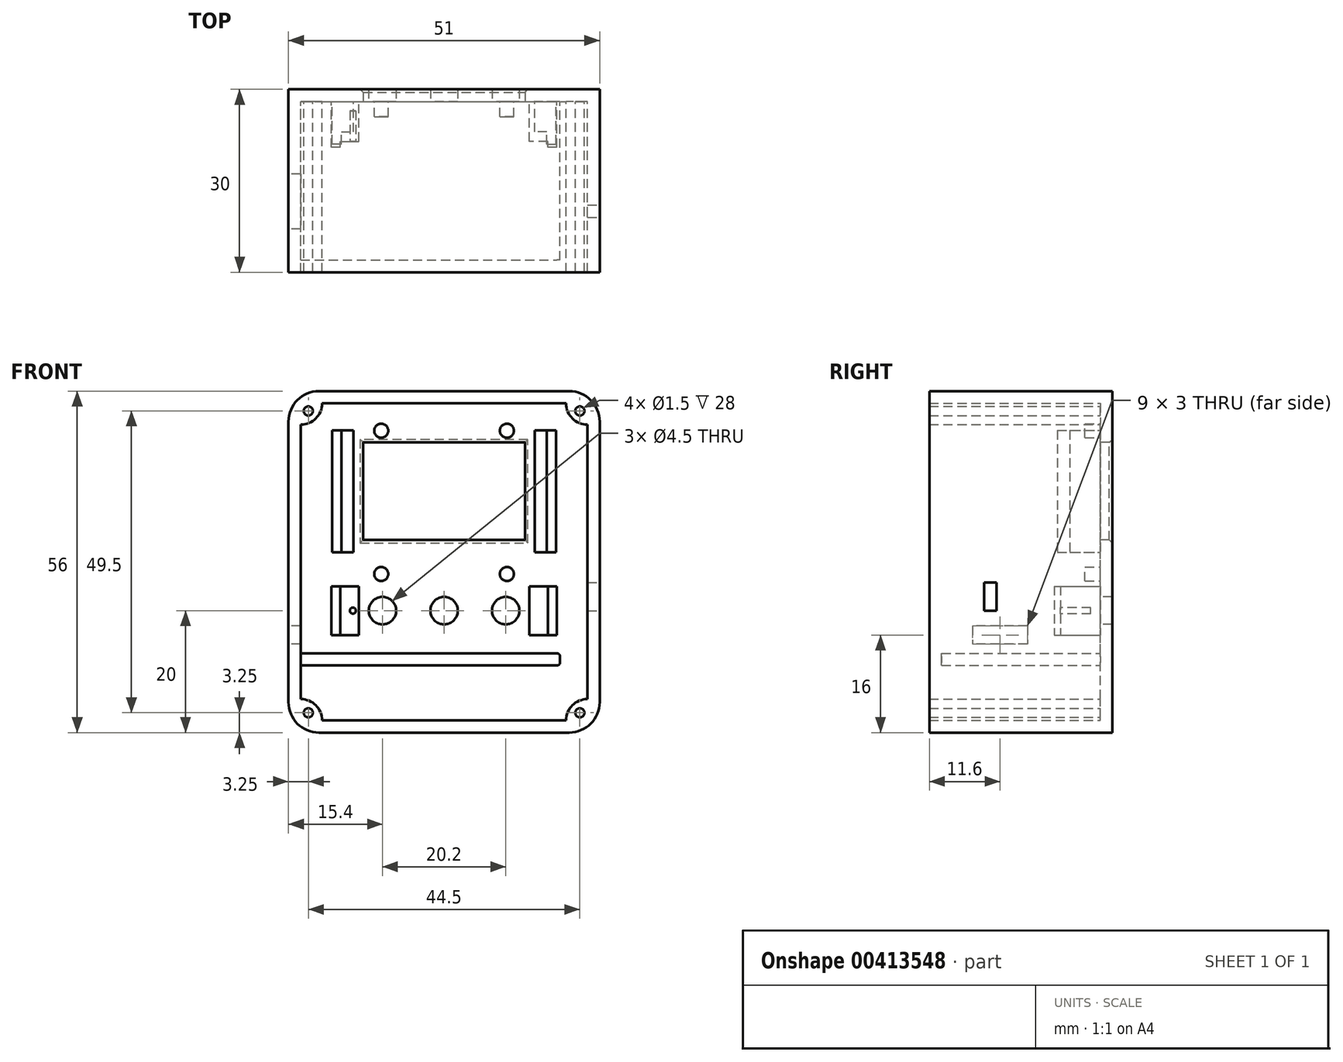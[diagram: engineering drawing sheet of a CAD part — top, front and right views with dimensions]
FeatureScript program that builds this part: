
annotation { "Feature Type Name" : "Feature", "Feature Type Description" : "" }
export const myFeature = defineFeature(function(context is Context, id is Id, definition is map)
    precondition{}
    {
        {
            var Q0;
            Q0=qCreatedBy(makeId("Front.planeOp"),FACE);
            var sketch = newSketch(context, id + "F0", { "sketchPlane" : qUnion([Q0])});
            skLineSegment(sketch, "E0.bottom", {"start": v(0, 0) * mm, "end": v(51, 0) * mm});
            skLineSegment(sketch, "E0.top", {"start": v(0, 56) * mm, "end": v(51, 56) * mm});
            skLineSegment(sketch, "E0.left", {"start": v(0, 0) * mm, "end": v(0, 56) * mm});
            skLineSegment(sketch, "E0.right", {"start": v(51, 0) * mm, "end": v(51, 56) * mm});
            skLineSegment(sketch, "E1", {"start": v(-7.83, 28) * mm, "end": v(58.94, 28) * mm, "construction": true});
            skPoint(sketch, "E1.startSnap0", {"position": v(0, 28) * mm});
            skPoint(sketch, "E1.endSnap0", {"position": v(51, 28) * mm});
            skSolve(sketch);
        }
        {
            var Q0;
            Q0 = qSketchRegion(id + "F0", true);
            extrude(context, id + "F1", {"entities" : qUnion([Q0]), "depth" : 30 * mm});
        }
        {
            var Q0;
            Q0=makeQuery(id+"F1.opExtrude","CAP_FACE",FACE,{"disambiguationData":[OSD([sQuery(id+"F0.wireOp",EDGE,"E0.bottom"),sQuery(id+"F0.wireOp",EDGE,"E0.top"),sQuery(id+"F0.wireOp",EDGE,"E0.left"),sQuery(id+"F0.wireOp",EDGE,"E0.right")])],"isStart":false});
            shell(context, id + "F2", {"entities" : qUnion([Q0]), "thickness" : 2 * mm});
        }
        {
            var Q0;
            Q0=makeQuery(id+"F1.opExtrude","SWEPT_EDGE",EDGE,{"disambiguationData":[OSD([sQuery(id+"F0.wireOp",EDGE,"E0.top"),sQuery(id+"F0.wireOp",EDGE,"E0.left")])]});
            var Q1;
            Q1=makeQuery(id+"F1.opExtrude","SWEPT_EDGE",EDGE,{"disambiguationData":[OSD([sQuery(id+"F0.wireOp",EDGE,"E0.bottom"),sQuery(id+"F0.wireOp",EDGE,"E0.left")])]});
            var Q2;
            Q2=makeQuery(id+"F1.opExtrude","SWEPT_EDGE",EDGE,{"disambiguationData":[OSD([sQuery(id+"F0.wireOp",EDGE,"E0.bottom"),sQuery(id+"F0.wireOp",EDGE,"E0.right")])]});
            var Q3;
            Q3=makeQuery(id+"F1.opExtrude","SWEPT_EDGE",EDGE,{"disambiguationData":[OSD([sQuery(id+"F0.wireOp",EDGE,"E0.top"),sQuery(id+"F0.wireOp",EDGE,"E0.right")])]});
            fillet(context, id + "F3", {"entities" : qUnion([Q0, Q1, Q2, Q3]), "radius" : 5 * mm, "tangentPropagation" : true, "allowEdgeOverflow" : false});
        }
        {
            var Q0;
            Q0=makeQuery(id+"F2.opShell","OFFSET_FACE",FACE,{"disambiguationData":[OSD([sQuery(id+"F0.wireOp",EDGE,"E0.bottom"),sQuery(id+"F0.wireOp",EDGE,"E0.top"),sQuery(id+"F0.wireOp",EDGE,"E0.left"),sQuery(id+"F0.wireOp",EDGE,"E0.right")])]});
            var sketch = newSketch(context, id + "F4", { "sketchPlane" : qUnion([Q0])});
            skLineSegment(sketch, "E2.bottom", {"start": v(12.25, 47.58) * mm, "end": v(38.75, 47.58) * mm});
            skLineSegment(sketch, "E2.top", {"start": v(12.25, 31.58) * mm, "end": v(38.75, 31.58) * mm});
            skLineSegment(sketch, "E2.left", {"start": v(12.25, 47.58) * mm, "end": v(12.25, 31.58) * mm});
            skLineSegment(sketch, "E2.right", {"start": v(38.75, 47.58) * mm, "end": v(38.75, 31.58) * mm});
            skSolve(sketch);
        }
        {
            var Q0;
            Q0=makeQuery(id+"F4.imprint","IMPRINT",FACE,{"disambiguationData":[TD([[makeQuery(id+"F4.imprint","IMPRINT",EDGE,{"derivedFrom":sQuery(id+"F4.wireOp",EDGE,"E2.bottom")}),-1.0]])]});
            extrude(context, id + "F5", {"entities" : qUnion([Q0]), "operationType" : NewBodyOperationType.REMOVE, "endBound" : BoundingType.THROUGH_ALL, "oppositeDirection" : true, "depth" : 25 * mm});
        }
        {
            var Q0;
            Q0=makeQuery(id+"F5.boolean.opBoolean","INTERSECT",EDGE,{"derivedFrom":[makeQuery(id+"F1.opExtrude","CAP_FACE",FACE,{"disambiguationData":[OSD([sQuery(id+"F0.wireOp",EDGE,"E0.bottom"),sQuery(id+"F0.wireOp",EDGE,"E0.top"),sQuery(id+"F0.wireOp",EDGE,"E0.left"),sQuery(id+"F0.wireOp",EDGE,"E0.right")])],"isStart":true}),makeQuery(id+"F5.opExtrude","SWEPT_FACE",FACE,{"disambiguationData":[OSD([sQuery(id+"F4.wireOp",EDGE,"E2.bottom")])]})]});
            var Q1;
            Q1=makeQuery(id+"F5.boolean.opBoolean","INTERSECT",EDGE,{"derivedFrom":[makeQuery(id+"F1.opExtrude","CAP_FACE",FACE,{"disambiguationData":[OSD([sQuery(id+"F0.wireOp",EDGE,"E0.bottom"),sQuery(id+"F0.wireOp",EDGE,"E0.top"),sQuery(id+"F0.wireOp",EDGE,"E0.left"),sQuery(id+"F0.wireOp",EDGE,"E0.right")])],"isStart":true}),makeQuery(id+"F5.opExtrude","SWEPT_FACE",FACE,{"disambiguationData":[OSD([sQuery(id+"F4.wireOp",EDGE,"E2.right")])]})]});
            var Q2;
            Q2=makeQuery(id+"F5.boolean.opBoolean","INTERSECT",EDGE,{"derivedFrom":[makeQuery(id+"F1.opExtrude","CAP_FACE",FACE,{"disambiguationData":[OSD([sQuery(id+"F0.wireOp",EDGE,"E0.bottom"),sQuery(id+"F0.wireOp",EDGE,"E0.top"),sQuery(id+"F0.wireOp",EDGE,"E0.left"),sQuery(id+"F0.wireOp",EDGE,"E0.right")])],"isStart":true}),makeQuery(id+"F5.opExtrude","SWEPT_FACE",FACE,{"disambiguationData":[OSD([sQuery(id+"F4.wireOp",EDGE,"E2.top")])]})]});
            var Q3;
            Q3=makeQuery(id+"F5.boolean.opBoolean","INTERSECT",EDGE,{"derivedFrom":[makeQuery(id+"F1.opExtrude","CAP_FACE",FACE,{"disambiguationData":[OSD([sQuery(id+"F0.wireOp",EDGE,"E0.bottom"),sQuery(id+"F0.wireOp",EDGE,"E0.top"),sQuery(id+"F0.wireOp",EDGE,"E0.left"),sQuery(id+"F0.wireOp",EDGE,"E0.right")])],"isStart":true}),makeQuery(id+"F5.opExtrude","SWEPT_FACE",FACE,{"disambiguationData":[OSD([sQuery(id+"F4.wireOp",EDGE,"E2.left")])]})]});
            chamfer(context, id + "F6", {"entities" : qUnion([Q0, Q1, Q2, Q3]), "width" : 0.5 * mm, "tangentPropagation" : true});
        }
        {
            var Q0;
            Q0=makeQuery(id+"F2.opShell","OFFSET_FACE",FACE,{"disambiguationData":[OSD([sQuery(id+"F0.wireOp",EDGE,"E0.bottom"),sQuery(id+"F0.wireOp",EDGE,"E0.top"),sQuery(id+"F0.wireOp",EDGE,"E0.left"),sQuery(id+"F0.wireOp",EDGE,"E0.right")])]});
            var sketch = newSketch(context, id + "F7", { "sketchPlane" : qUnion([Q0])});
            skLineSegment(sketch, "E3.bottom", {"start": v(2, 13) * mm, "end": v(44.5, 13) * mm});
            skLineSegment(sketch, "E3.top", {"start": v(2, 11) * mm, "end": v(44.5, 11) * mm});
            skLineSegment(sketch, "E3.left", {"start": v(2, 13) * mm, "end": v(2, 11) * mm});
            skLineSegment(sketch, "E3.right", {"start": v(44.5, 13) * mm, "end": v(44.5, 11) * mm});
            skSolve(sketch);
        }
        {
            var Q0;
            Q0 = qSketchRegion(id + "F7", true);
            extrude(context, id + "F8", {"entities" : qUnion([Q0]), "operationType" : NewBodyOperationType.ADD, "depth" : 26 * mm});
        }
        {
            var Q0;
            Q0=makeQuery(id+"F8.opExtrude","SWEPT_EDGE",EDGE,{"disambiguationData":[OSD([sQuery(id+"F7.wireOp",EDGE,"E3.top"),sQuery(id+"F7.wireOp",EDGE,"E3.right")])]});
            var Q1;
            Q1=makeQuery(id+"F8.opExtrude","SWEPT_EDGE",EDGE,{"disambiguationData":[OSD([sQuery(id+"F7.wireOp",EDGE,"E3.bottom"),sQuery(id+"F7.wireOp",EDGE,"E3.right")])]});
            fillet(context, id + "F9", {"entities" : qUnion([Q0, Q1]), "radius" : 0.5 * mm, "tangentPropagation" : true, "allowEdgeOverflow" : false});
        }
        {
            var Q0;
            Q0=makeQuery(id+"F1.opExtrude","SWEPT_FACE",FACE,{"disambiguationData":[OSD([sQuery(id+"F0.wireOp",EDGE,"E0.left")])]});
            var sketch = newSketch(context, id + "F10", { "sketchPlane" : qUnion([Q0])});
            skLineSegment(sketch, "E4.bottom", {"start": v(13.9, 17.5) * mm, "end": v(22.9, 17.5) * mm});
            skLineSegment(sketch, "E4.top", {"start": v(13.9, 14.5) * mm, "end": v(22.9, 14.5) * mm});
            skLineSegment(sketch, "E4.left", {"start": v(13.9, 17.5) * mm, "end": v(13.9, 14.5) * mm});
            skLineSegment(sketch, "E4.right", {"start": v(22.9, 17.5) * mm, "end": v(22.9, 14.5) * mm});
            skSolve(sketch);
        }
        {
            var Q0;
            Q0 = qSketchRegion(id + "F10", true);
            extrude(context, id + "F11", {"entities" : qUnion([Q0]), "operationType" : NewBodyOperationType.REMOVE, "oppositeDirection" : true, "depth" : 3 * mm});
        }
        {
            var Q0;
            Q0=makeQuery(id+"F2.opShell","OFFSET_FACE",FACE,{"disambiguationData":[OSD([sQuery(id+"F0.wireOp",EDGE,"E0.bottom"),sQuery(id+"F0.wireOp",EDGE,"E0.top"),sQuery(id+"F0.wireOp",EDGE,"E0.left"),sQuery(id+"F0.wireOp",EDGE,"E0.right")])]});
            var sketch = newSketch(context, id + "F12", { "sketchPlane" : qUnion([Q0])});
            skLineSegment(sketch, "E5.bottom", {"start": v(8.65, 49.58) * mm, "end": v(10.65, 49.58) * mm});
            skLineSegment(sketch, "E5.top", {"start": v(8.65, 29.58) * mm, "end": v(10.65, 29.58) * mm});
            skLineSegment(sketch, "E5.left", {"start": v(8.65, 49.58) * mm, "end": v(8.65, 29.58) * mm});
            skLineSegment(sketch, "E5.right", {"start": v(10.65, 49.58) * mm, "end": v(10.65, 29.58) * mm});
            skLineSegment(sketch, "E6", {"start": v(25.5, 62.72) * mm, "end": v(25.5, -6.22) * mm, "construction": true});
            skPoint(sketch, "E6.startSnap0", {"position": v(25.5, 54) * mm});
            skLineSegment(sketch, "E7", {"start": v(59.51, 39.58) * mm, "end": v(-4.9, 39.58) * mm, "construction": true});
            skPoint(sketch, "E7.startSnap0", {"position": v(38.75, 39.58) * mm});
            skLineSegment(sketch, "E8.MirrorCS", {"start": v(40.35, 49.58) * mm, "end": v(40.35, 29.58) * mm});
            skLineSegment(sketch, "E9.MirrorCS", {"start": v(42.35, 29.58) * mm, "end": v(40.35, 29.58) * mm});
            skLineSegment(sketch, "E10.MirrorCS", {"start": v(42.35, 49.58) * mm, "end": v(40.35, 49.58) * mm});
            skLineSegment(sketch, "E11.MirrorCS", {"start": v(42.35, 49.58) * mm, "end": v(42.35, 29.58) * mm});
            skLineSegment(sketch, "E12.bottom", {"start": v(8.65, 49.58) * mm, "end": v(7.15, 49.58) * mm});
            skLineSegment(sketch, "E12.top", {"start": v(8.65, 29.58) * mm, "end": v(7.15, 29.58) * mm});
            skLineSegment(sketch, "E12.right", {"start": v(7.15, 49.58) * mm, "end": v(7.15, 29.58) * mm});
            skLineSegment(sketch, "E13.MirrorCS", {"start": v(42.35, 29.58) * mm, "end": v(43.85, 29.58) * mm});
            skLineSegment(sketch, "E14.MirrorCS", {"start": v(42.35, 49.58) * mm, "end": v(43.85, 49.58) * mm});
            skLineSegment(sketch, "E15.MirrorCS", {"start": v(43.85, 49.58) * mm, "end": v(43.85, 29.58) * mm});
            skSolve(sketch);
        }
        {
            var Q0;
            Q0=makeQuery(id+"F12.imprint","IMPRINT",FACE,{"disambiguationData":[TD([[makeQuery(id+"F12.imprint","IMPRINT",EDGE,{"derivedFrom":sQuery(id+"F12.wireOp",EDGE,"E5.bottom")}),-1.0]])]});
            var Q1;
            Q1=makeQuery(id+"F12.imprint","IMPRINT",FACE,{"disambiguationData":[TD([[makeQuery(id+"F12.imprint","IMPRINT",EDGE,{"derivedFrom":sQuery(id+"F12.wireOp",EDGE,"E8.MirrorCS")}),1.0]])]});
            extrude(context, id + "F13", {"entities" : qUnion([Q0, Q1]), "operationType" : NewBodyOperationType.ADD, "depth" : 5 * mm});
        }
        {
            var Q0;
            Q0=makeQuery(id+"F12.imprint","IMPRINT",FACE,{"disambiguationData":[TD([[makeQuery(id+"F12.imprint","IMPRINT",EDGE,{"derivedFrom":sQuery(id+"F12.wireOp",EDGE,"E12.bottom")}),1.0]])]});
            var Q1;
            Q1=makeQuery(id+"F12.imprint","IMPRINT",FACE,{"disambiguationData":[TD([[makeQuery(id+"F12.imprint","IMPRINT",EDGE,{"derivedFrom":sQuery(id+"F12.wireOp",EDGE,"E11.MirrorCS")}),1.0]])]});
            extrude(context, id + "F14", {"entities" : qUnion([Q0, Q1]), "operationType" : NewBodyOperationType.ADD, "depth" : 7 * mm});
        }
        {
            var Q0;
            Q0=makeQuery(id+"F12.imprint","IMPRINT",FACE,{"disambiguationData":[TD([[makeQuery(id+"F12.imprint","IMPRINT",EDGE,{"derivedFrom":sQuery(id+"F12.wireOp",EDGE,"E5.bottom")}),1.0]])]});
            var sketch = newSketch(context, id + "F15", { "sketchPlane" : qUnion([Q0])});
            skLineSegment(sketch, "E16.bottom", {"start": v(8.5, 24) * mm, "end": v(11.5, 24) * mm});
            skLineSegment(sketch, "E16.left", {"start": v(8.5, 24) * mm, "end": v(8.5, 16) * mm});
            skLineSegment(sketch, "E16.right", {"start": v(11.5, 24) * mm, "end": v(11.5, 16) * mm});
            skLineSegment(sketch, "E17", {"start": v(8.5, 16) * mm, "end": v(11.5, 16) * mm});
            skLineSegment(sketch, "E18.MirrorCS", {"start": v(42.5, 16) * mm, "end": v(39.5, 16) * mm});
            skLineSegment(sketch, "E19.MirrorCS", {"start": v(39.5, 24) * mm, "end": v(39.5, 16) * mm});
            skLineSegment(sketch, "E20.MirrorCS", {"start": v(42.5, 24) * mm, "end": v(42.5, 16) * mm});
            skLineSegment(sketch, "E21.MirrorCS", {"start": v(42.5, 24) * mm, "end": v(39.5, 24) * mm});
            skLineSegment(sketch, "E22", {"start": v(8.5, 24) * mm, "end": v(7, 24) * mm});
            skLineSegment(sketch, "E23", {"start": v(7, 24) * mm, "end": v(7, 16) * mm});
            skLineSegment(sketch, "E24", {"start": v(7, 16) * mm, "end": v(8.5, 16) * mm});
            skLineSegment(sketch, "E25.MirrorCS", {"start": v(44, 16) * mm, "end": v(42.5, 16) * mm});
            skLineSegment(sketch, "E26.MirrorCS", {"start": v(42.5, 24) * mm, "end": v(44, 24) * mm});
            skLineSegment(sketch, "E27.MirrorCS", {"start": v(44, 24) * mm, "end": v(44, 16) * mm});
            skSolve(sketch);
        }
        {
            var Q0;
            Q0=makeQuery(id+"F15.imprint","IMPRINT",FACE,{"disambiguationData":[TD([[makeQuery(id+"F15.imprint","IMPRINT",EDGE,{"derivedFrom":sQuery(id+"F15.wireOp",EDGE,"E16.bottom")}),-1.0]])]});
            var Q1;
            Q1=makeQuery(id+"F15.imprint","IMPRINT",FACE,{"disambiguationData":[TD([[makeQuery(id+"F15.imprint","IMPRINT",EDGE,{"derivedFrom":sQuery(id+"F15.wireOp",EDGE,"E18.MirrorCS")}),-1.0]])]});
            extrude(context, id + "F16", {"entities" : qUnion([Q0, Q1]), "operationType" : NewBodyOperationType.ADD, "depth" : 6.54 * mm});
        }
        {
            var Q0;
            Q0=makeQuery(id+"F12.imprint","IMPRINT",FACE,{"disambiguationData":[TD([[makeQuery(id+"F12.imprint","IMPRINT",EDGE,{"derivedFrom":sQuery(id+"F12.wireOp",EDGE,"E5.bottom")}),1.0]])]});
            var sketch = newSketch(context, id + "F17", { "sketchPlane" : qUnion([Q0])});
            skCircle(sketch, "E28", {"center": v(15.4, 20) * mm, "radius": 2.25 * mm});
            skCircle(sketch, "E29", {"center": v(25.5, 20) * mm, "radius": 2.25 * mm});
            skCircle(sketch, "E30", {"center": v(35.6, 20) * mm, "radius": 2.25 * mm});
            skSolve(sketch);
        }
        {
            var Q0;
            Q0 = qSketchRegion(id + "F17", true);
            extrude(context, id + "F18", {"entities" : qUnion([Q0]), "operationType" : NewBodyOperationType.REMOVE, "endBound" : BoundingType.THROUGH_ALL, "oppositeDirection" : true, "depth" : 25 * mm});
        }
        {
            var Q0;
            Q0=makeQuery(id+"F15.imprint","IMPRINT",FACE,{"disambiguationData":[TD([[makeQuery(id+"F15.imprint","IMPRINT",EDGE,{"derivedFrom":sQuery(id+"F15.wireOp",EDGE,"E16.left")}),-1.0]])]});
            var Q1;
            Q1=makeQuery(id+"F15.imprint","IMPRINT",FACE,{"disambiguationData":[TD([[makeQuery(id+"F15.imprint","IMPRINT",EDGE,{"derivedFrom":sQuery(id+"F15.wireOp",EDGE,"E20.MirrorCS")}),1.0]])]});
            extrude(context, id + "F19", {"entities" : qUnion([Q0, Q1]), "operationType" : NewBodyOperationType.ADD, "depth" : 7.54 * mm});
        }
        {
            var Q0;
            Q0=makeQuery(id+"F16.opExtrude","CAP_FACE",FACE,{"disambiguationData":[OSD([sQuery(id+"F15.wireOp",EDGE,"E16.bottom"),sQuery(id+"F15.wireOp",EDGE,"E16.left"),sQuery(id+"F15.wireOp",EDGE,"E16.right"),sQuery(id+"F15.wireOp",EDGE,"E17")])],"isStart":false});
            var sketch = newSketch(context, id + "F20", { "sketchPlane" : qUnion([Q0])});
            skCircle(sketch, "E31", {"center": v(10.55, 20) * mm, "radius": 0.5 * mm});
            skCircle(sketch, "E32.MirrorC", {"center": v(40.45, 20) * mm, "radius": 0.5 * mm});
            skSolve(sketch);
        }
        {
            var Q0;
            Q0=makeQuery(id+"F20.imprint","IMPRINT",FACE,{"disambiguationData":[TD([[makeQuery(id+"F20.imprint","IMPRINT",EDGE,{"derivedFrom":sQuery(id+"F20.wireOp",EDGE,"E31")}),1.0]])]});
            var Q1;
            Q1=makeQuery(id+"F20.imprint","IMPRINT",FACE,{"disambiguationData":[TD([[makeQuery(id+"F20.imprint","IMPRINT",EDGE,{"derivedFrom":sQuery(id+"F20.wireOp",EDGE,"E32.MirrorC")}),-1.0]])]});
            extrude(context, id + "F21", {"entities" : qUnion([Q0, Q1]), "operationType" : NewBodyOperationType.REMOVE, "oppositeDirection" : true, "depth" : 5 * mm});
        }
        {
            var Q0;
            {var subQ3=sQuery(id+"F7.wireOp",EDGE,"E3.bottom");Q0=makeQuery(id+"F7.imprint","IMPRINT",FACE,{"disambiguationData":[TD([[makeQuery(id+"F7.imprint","IMPRINT",EDGE,{"derivedFrom":subQ3}),1.0]])]});}
            var sketch = newSketch(context, id + "F22", { "sketchPlane" : qUnion([Q0])});
            skCircle(sketch, "E33", {"center": v(15.2, 49.5) * mm, "radius": 1.15 * mm});
            skCircle(sketch, "E34", {"center": v(35.8, 49.5) * mm, "radius": 1.15 * mm});
            skCircle(sketch, "E35.MirrorC", {"center": v(35.8, 26) * mm, "radius": 1.15 * mm});
            skCircle(sketch, "E36.MirrorC", {"center": v(15.2, 26) * mm, "radius": 1.15 * mm});
            skSolve(sketch);
        }
        {
            var Q0;
            Q0 = qSketchRegion(id + "F22", true);
            extrude(context, id + "F23", {"entities" : qUnion([Q0]), "operationType" : NewBodyOperationType.ADD, "depth" : 2.5 * mm});
        }
        {
            var Q0;
            {var subQ3=sQuery(id+"F7.wireOp",EDGE,"E3.bottom");Q0=makeQuery(id+"F7.imprint","IMPRINT",FACE,{"disambiguationData":[TD([[makeQuery(id+"F7.imprint","IMPRINT",EDGE,{"derivedFrom":subQ3}),1.0]])]});}
            var sketch = newSketch(context, id + "F24", { "sketchPlane" : qUnion([Q0])});
            skLineSegment(sketch, "E37.bottom", {"start": v(2, 54) * mm, "end": v(5.5, 54) * mm});
            skLineSegment(sketch, "E37.left", {"start": v(2, 54) * mm, "end": v(2, 50.5) * mm});
            skArc(sketch, "E38", {"start": v(2, 50.5) * mm, "mid": v(4.47, 51.53) * mm, "end": v(5.5, 54) * mm});
            skCircle(sketch, "E39", {"center": v(3.25, 52.75) * mm, "radius": 0.75 * mm});
            skLineSegment(sketch, "E40.MirrorCS", {"start": v(49, 54) * mm, "end": v(49, 50.5) * mm});
            skLineSegment(sketch, "E41.MirrorCS", {"start": v(49, 54) * mm, "end": v(45.5, 54) * mm});
            skArc(sketch, "E42.MirrorCS", {"start": v(49, 50.5) * mm, "mid": v(46.53, 51.53) * mm, "end": v(45.5, 54) * mm});
            skCircle(sketch, "E43.MirrorC", {"center": v(47.75, 52.75) * mm, "radius": 0.75 * mm});
            skCircle(sketch, "E44.MirrorC", {"center": v(47.75, 3.25) * mm, "radius": 0.75 * mm});
            skLineSegment(sketch, "E45.MirrorCS", {"start": v(49, 2) * mm, "end": v(49, 5.5) * mm});
            skLineSegment(sketch, "E46.MirrorCS", {"start": v(49, 2) * mm, "end": v(45.5, 2) * mm});
            skArc(sketch, "E47.MirrorCS", {"start": v(49, 5.5) * mm, "mid": v(46.53, 4.47) * mm, "end": v(45.5, 2) * mm});
            skLineSegment(sketch, "E48.MirrorCS", {"start": v(2, 2) * mm, "end": v(2, 5.5) * mm});
            skLineSegment(sketch, "E49.MirrorCS", {"start": v(2, 2) * mm, "end": v(5.5, 2) * mm});
            skCircle(sketch, "E50.MirrorC", {"center": v(3.25, 3.25) * mm, "radius": 0.75 * mm});
            skArc(sketch, "E51.MirrorCS", {"start": v(2, 5.5) * mm, "mid": v(4.47, 4.47) * mm, "end": v(5.5, 2) * mm});
            skSolve(sketch);
        }
        {
            var Q0;
            Q0 = qSketchRegion(id + "F24", true);
            extrude(context, id + "F25", {"entities" : qUnion([Q0]), "operationType" : NewBodyOperationType.ADD, "depth" : 28 * mm});
        }
        {
            var Q0;
            Q0=makeQuery(id+"F1.opExtrude","SWEPT_FACE",FACE,{"disambiguationData":[OSD([sQuery(id+"F0.wireOp",EDGE,"E0.right")])]});
            var sketch = newSketch(context, id + "F26", { "sketchPlane" : qUnion([Q0])});
            skLineSegment(sketch, "E52.bottom", {"start": v(-21, 24.6) * mm, "end": v(-19, 24.6) * mm});
            skLineSegment(sketch, "E52.top", {"start": v(-21, 20) * mm, "end": v(-19, 20) * mm});
            skLineSegment(sketch, "E52.left", {"start": v(-21, 24.6) * mm, "end": v(-21, 20) * mm});
            skLineSegment(sketch, "E52.right", {"start": v(-19, 24.6) * mm, "end": v(-19, 20) * mm});
            skSolve(sketch);
        }
        {
            var Q0;
            Q0 = qSketchRegion(id + "F26", true);
            extrude(context, id + "F27", {"entities" : qUnion([Q0]), "operationType" : NewBodyOperationType.REMOVE, "oppositeDirection" : true, "depth" : 2 * mm});
        }
    });
